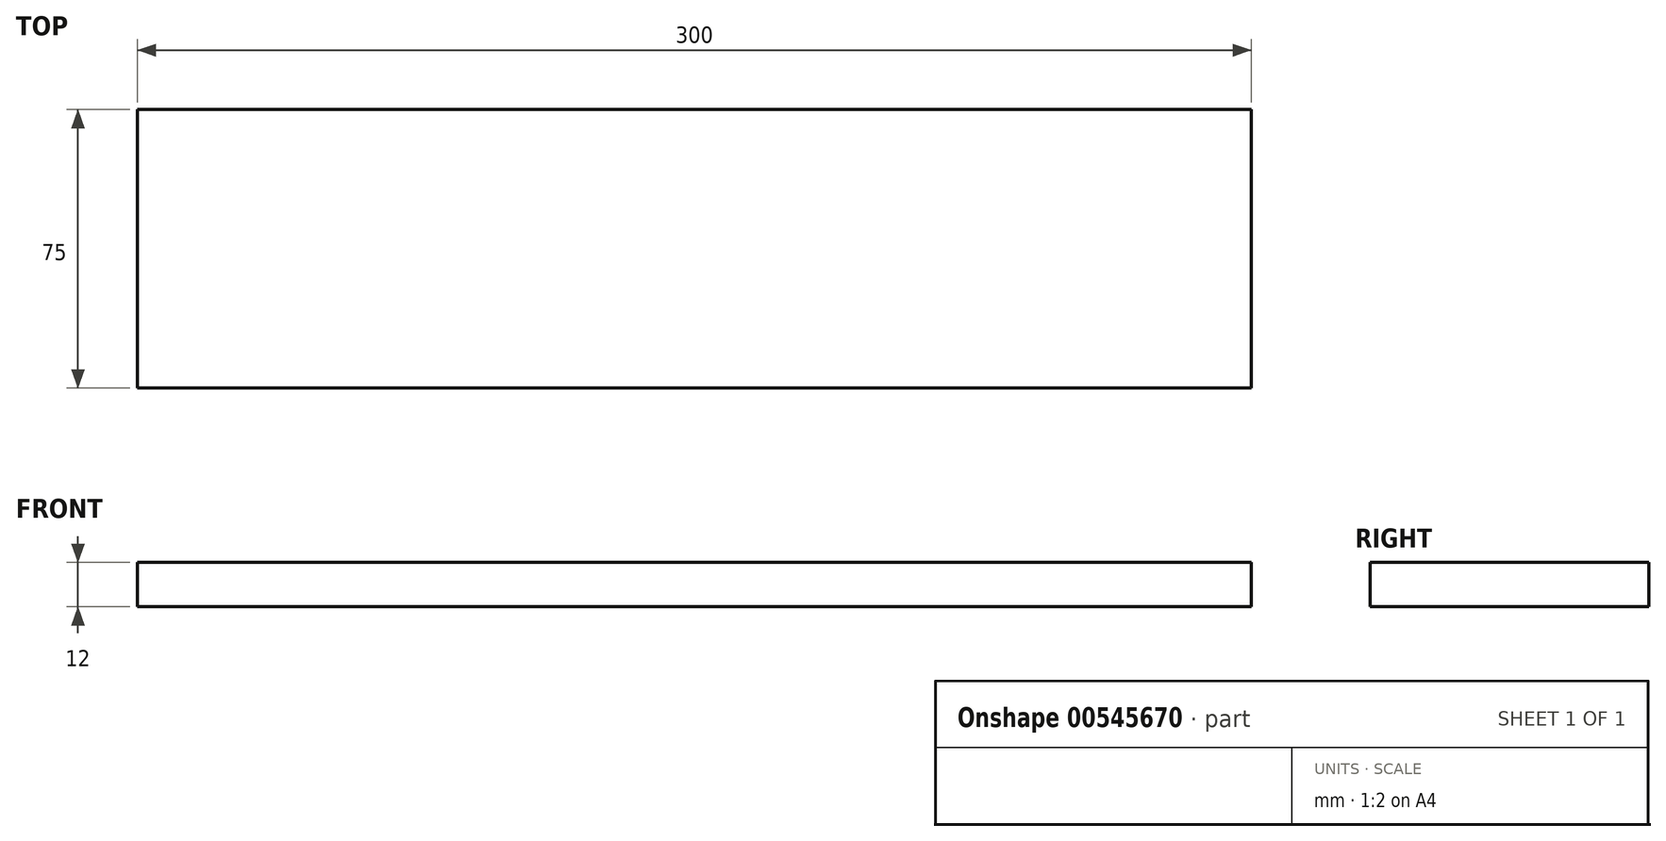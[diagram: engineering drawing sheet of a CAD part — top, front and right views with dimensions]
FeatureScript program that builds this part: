
annotation { "Feature Type Name" : "Feature", "Feature Type Description" : "" }
export const myFeature = defineFeature(function(context is Context, id is Id, definition is map)
    precondition{}
    {
        {
            var Q0;
            Q0=qCreatedBy(makeId("Top.planeOp"),FACE);
            var sketch = newSketch(context, id + "F0", { "sketchPlane" : qUnion([Q0])});
            skLineSegment(sketch, "E0.bottom", {"start": v(-150, 0) * mm, "end": v(150, 0) * mm});
            skLineSegment(sketch, "E0.top", {"start": v(-150, 75) * mm, "end": v(150, 75) * mm});
            skLineSegment(sketch, "E0.left", {"start": v(-150, 0) * mm, "end": v(-150, 75) * mm});
            skLineSegment(sketch, "E0.right", {"start": v(150, 0) * mm, "end": v(150, 75) * mm});
            skSolve(sketch);
        }
        {
            var Q0;
            Q0=makeQuery(id+"F0.imprint","IMPRINT",FACE,{"disambiguationData":[TD([[makeQuery(id+"F0.imprint","IMPRINT",EDGE,{"derivedFrom":sQuery(id+"F0.wireOp",EDGE,"E0.bottom")}),1.0]])]});
            extrude(context, id + "F1", {"entities" : qUnion([Q0]), "depth" : 12 * mm, "offsetDistance" : 25 * mm});
        }
    });
